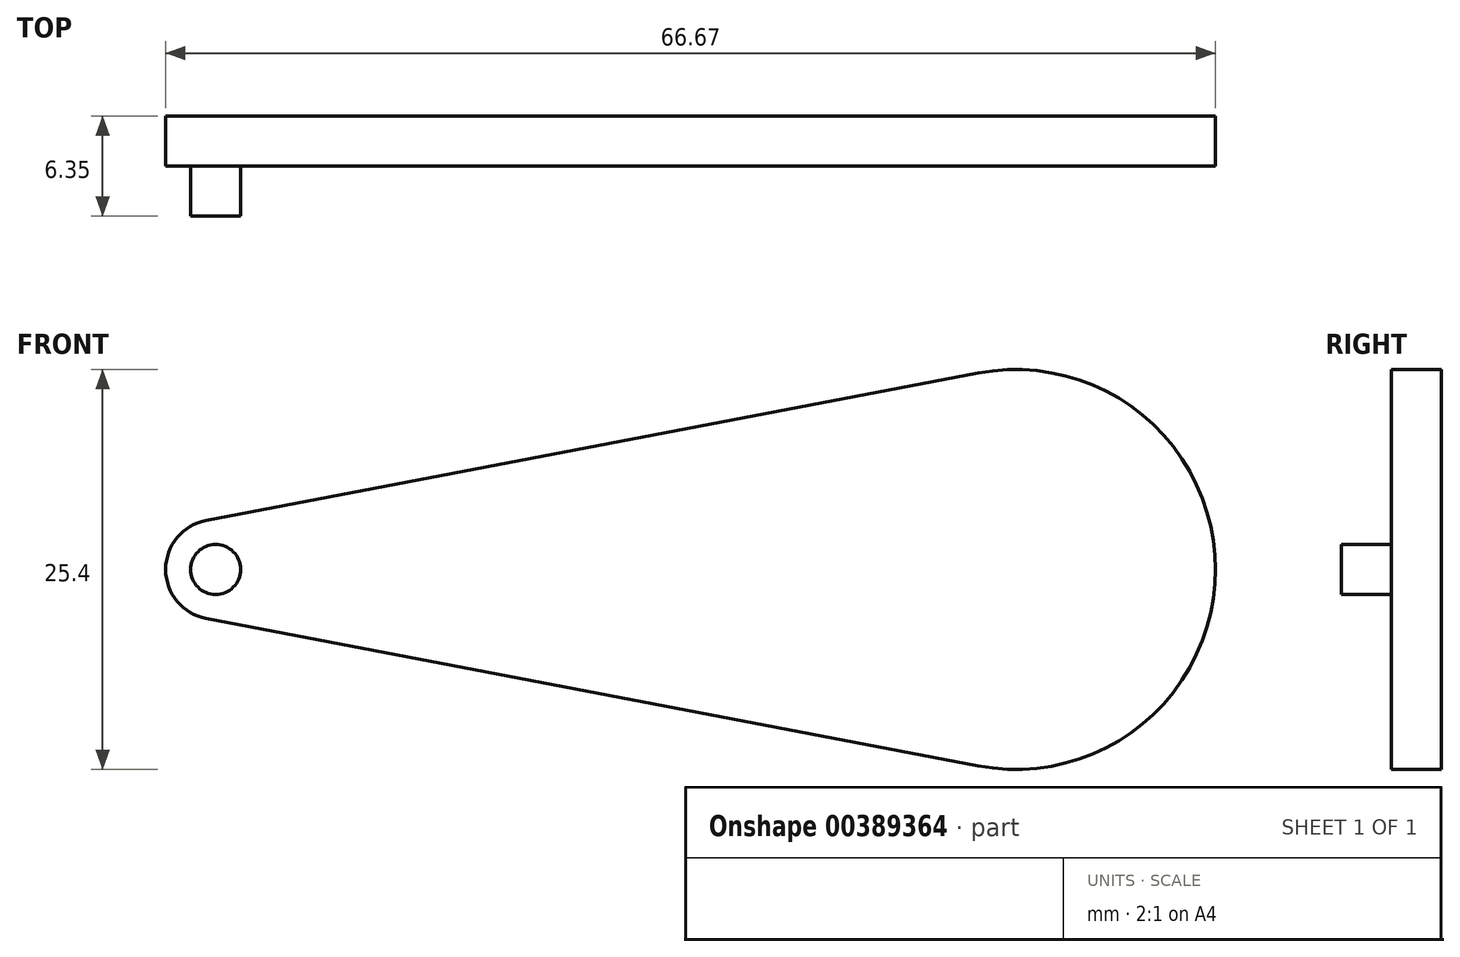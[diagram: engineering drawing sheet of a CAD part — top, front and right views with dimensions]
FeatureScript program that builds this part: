
annotation { "Feature Type Name" : "Feature", "Feature Type Description" : "" }
export const myFeature = defineFeature(function(context is Context, id is Id, definition is map)
    precondition{}
    {
        {
            var Q0;
            Q0=qCreatedBy(makeId("Front.planeOp"),FACE);
            var sketch = newSketch(context, id + "F0", { "sketchPlane" : qUnion([Q0])});
            skArc(sketch, "E0", {"start": v(-71.4, 3.12) * mm, "mid": v(-73.97, 0) * mm, "end": v(-71.4, -3.12) * mm});
            skArc(sketch, "E1", {"start": v(-22.38, -12.47) * mm, "mid": v(-7.3, 0) * mm, "end": v(-22.38, 12.47) * mm});
            skLineSegment(sketch, "E2", {"start": v(-71.4, 3.12) * mm, "end": v(-22.38, 12.47) * mm});
            skLineSegment(sketch, "E3", {"start": v(-71.4, -3.12) * mm, "end": v(-22.38, -12.47) * mm});
            skCircle(sketch, "E4", {"center": v(-70.8, 0) * mm, "radius": 3.18 * mm});
            skSolve(sketch);
        }
        {
            var Q0;
            Q0 = qSketchRegion(id + "F0", true);
            extrude(context, id + "F1", {"entities" : qUnion([Q0]), "depth" : 3.17 * mm});
        }
        {
            var Q0;
            Q0=makeQuery(id+"F1.opExtrude","CAP_FACE",FACE,{"disambiguationData":[OSD([sQuery(id+"F0.wireOp",EDGE,"E1"),sQuery(id+"F0.wireOp",EDGE,"E2"),sQuery(id+"F0.wireOp",EDGE,"E3"),sQuery(id+"F0.wireOp",EDGE,"E4")])],"isStart":false});
            var sketch = newSketch(context, id + "F2", { "sketchPlane" : qUnion([Q0])});
            skCircle(sketch, "E5", {"center": v(-70.8, 0) * mm, "radius": 1.59 * mm});
            skSolve(sketch);
        }
        {
            var Q0;
            Q0=makeQuery(id+"F2.imprint","IMPRINT",FACE,{"disambiguationData":[TD([[makeQuery(id+"F2.imprint","IMPRINT",EDGE,{"derivedFrom":sQuery(id+"F2.wireOp",EDGE,"E5")}),1.0]])]});
            extrude(context, id + "F3", {"entities" : qUnion([Q0]), "operationType" : NewBodyOperationType.ADD, "depth" : 3.17 * mm});
        }
    });
